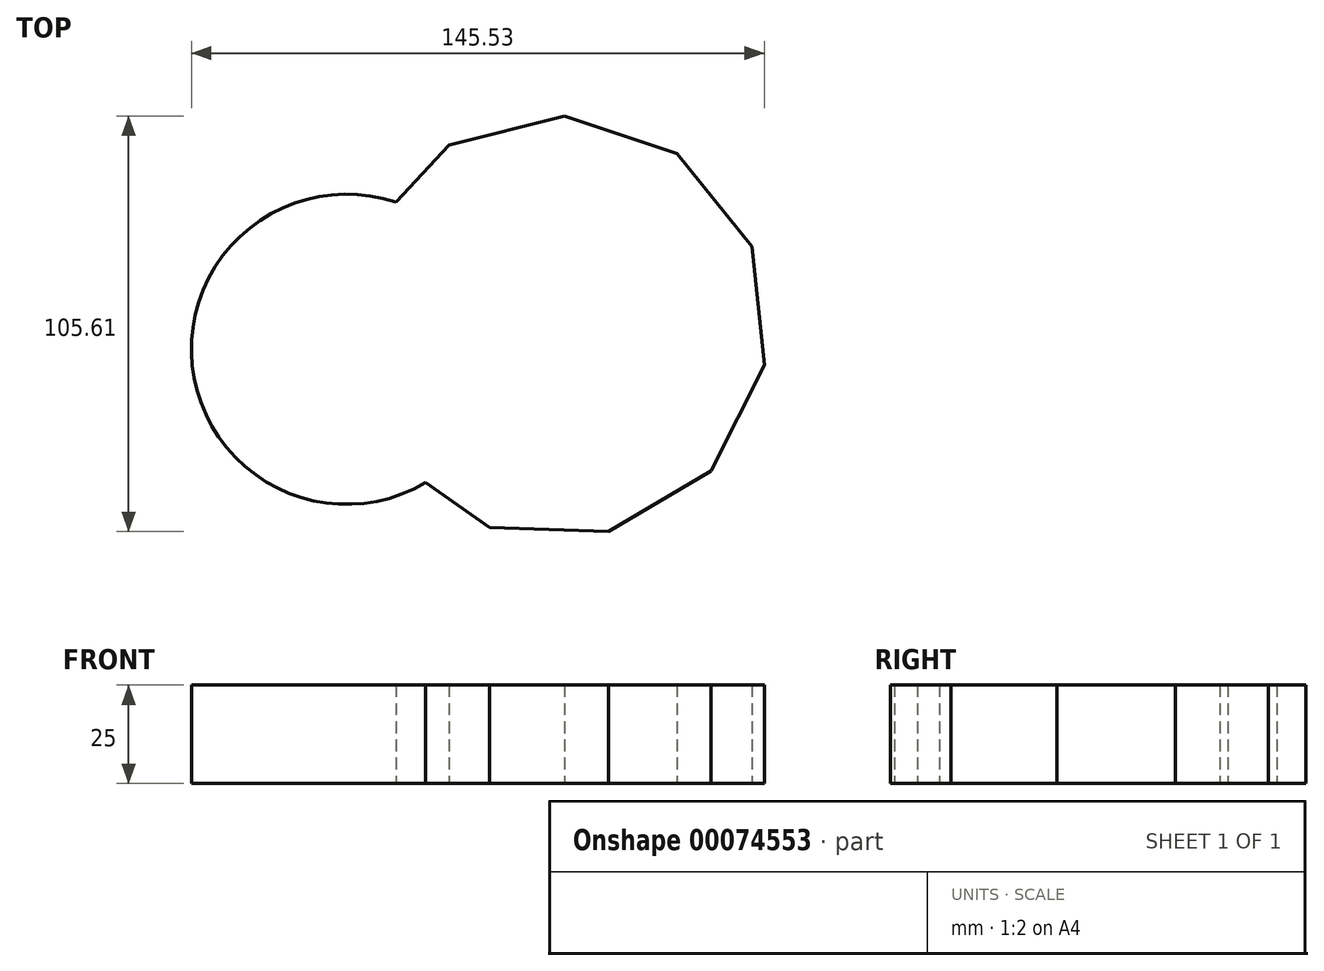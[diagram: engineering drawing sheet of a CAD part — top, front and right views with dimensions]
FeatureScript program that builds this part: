
annotation { "Feature Type Name" : "Feature", "Feature Type Description" : "" }
export const myFeature = defineFeature(function(context is Context, id is Id, definition is map)
    precondition{}
    {
        {
            var Q0;
            Q0=qCreatedBy(makeId("Top.planeOp"),FACE);
            var sketch = newSketch(context, id + "F0", { "sketchPlane" : qUnion([Q0])});
            skCircle(sketch, "E0.cCircle", {"center": v(42.24, 0) * mm, "radius": 51.48 * mm, "construction": true});
            skLineSegment(sketch, "E0.0", {"start": v(14.93, 46.18) * mm, "end": v(44.23, 53.61) * mm});
            skLineSegment(sketch, "E0.1", {"start": v(44.23, 53.61) * mm, "end": v(72.9, 44.02) * mm});
            skLineSegment(sketch, "E0.2", {"start": v(72.9, 44.02) * mm, "end": v(91.83, 20.46) * mm});
            skLineSegment(sketch, "E0.3", {"start": v(91.83, 20.46) * mm, "end": v(95.02, -9.6) * mm});
            skLineSegment(sketch, "E0.4", {"start": v(95.02, -9.6) * mm, "end": v(81.45, -36.62) * mm});
            skLineSegment(sketch, "E0.5", {"start": v(81.45, -36.62) * mm, "end": v(55.43, -52) * mm});
            skLineSegment(sketch, "E0.6", {"start": v(55.43, -52) * mm, "end": v(25.22, -50.88) * mm});
            skLineSegment(sketch, "E0.7", {"start": v(25.22, -50.88) * mm, "end": v(0.41, -33.6) * mm});
            skLineSegment(sketch, "E0.8", {"start": v(0.41, -33.6) * mm, "end": v(-11.11, -5.65) * mm});
            skLineSegment(sketch, "E0.9", {"start": v(-11.11, -5.65) * mm, "end": v(-5.7, 24.09) * mm});
            skLineSegment(sketch, "E0.10", {"start": v(-5.7, 24.09) * mm, "end": v(14.93, 46.18) * mm});
            skPoint(sketch, "E0.0.midPoint", {"position": v(29.58, 49.9) * mm});
            skCircle(sketch, "E1", {"center": v(-11.11, -5.65) * mm, "radius": 39.4 * mm});
            skSolve(sketch);
        }
        {
            var Q0;
            Q0 = qSketchRegion(id + "F0", true);
            extrude(context, id + "F1", {"entities" : qUnion([Q0]), "depth" : 25 * mm});
        }
    });
